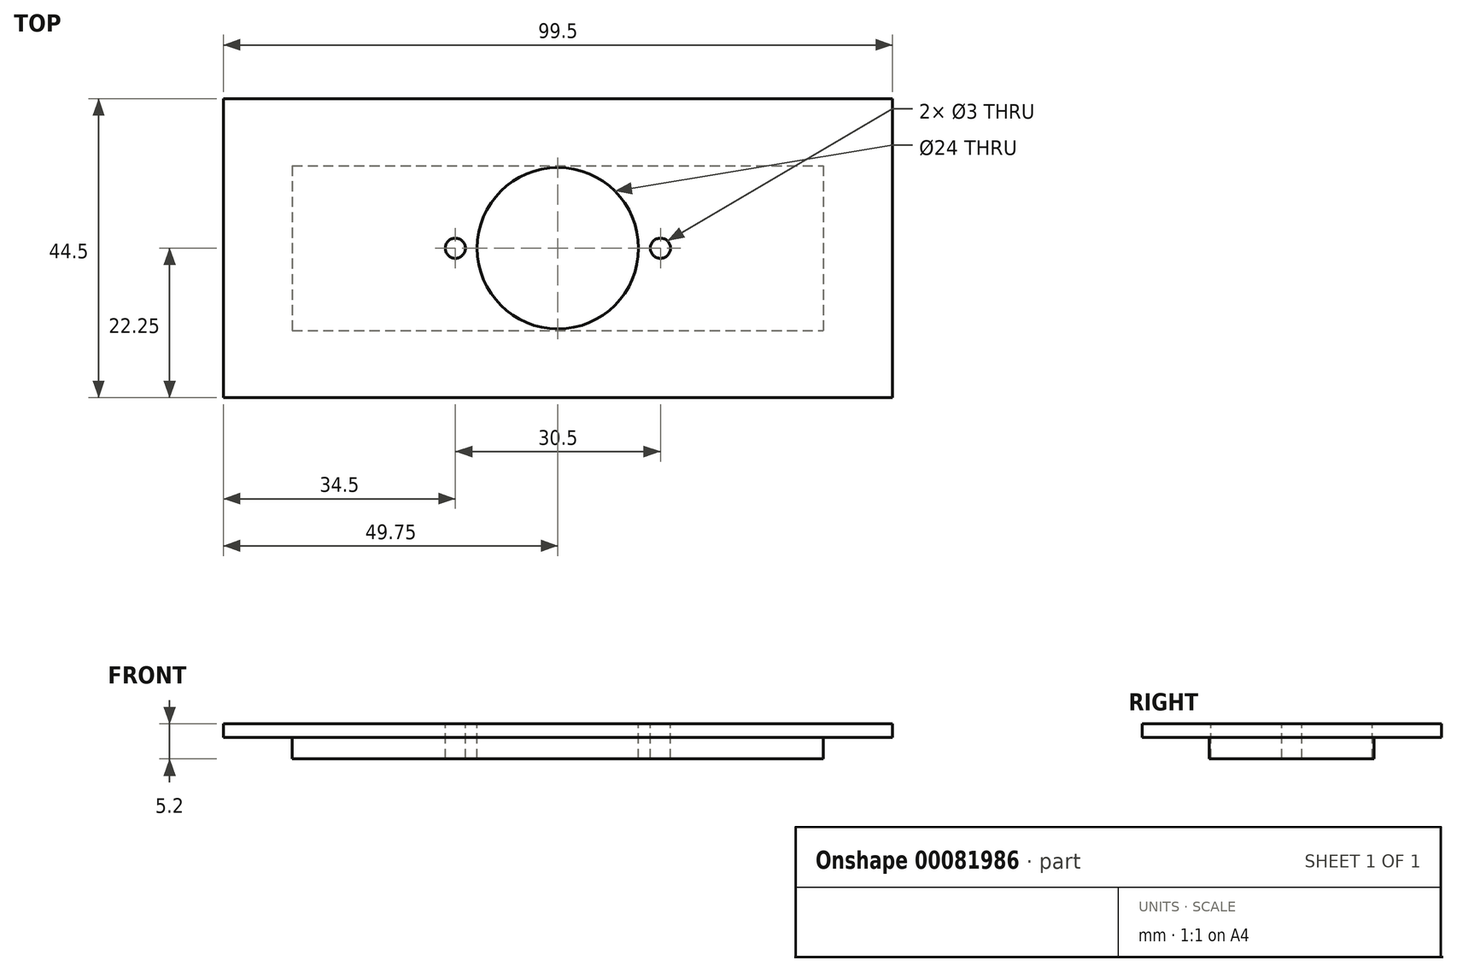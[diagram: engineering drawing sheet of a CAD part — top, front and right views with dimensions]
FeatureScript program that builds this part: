
annotation { "Feature Type Name" : "Feature", "Feature Type Description" : "" }
export const myFeature = defineFeature(function(context is Context, id is Id, definition is map)
    precondition{}
    {
        {
            var Q0;
            Q0=qCreatedBy(makeId("Top.planeOp"),FACE);
            var sketch = newSketch(context, id + "F0", { "sketchPlane" : qUnion([Q0])});
            skLineSegment(sketch, "E0.bottom", {"start": v(-39.5, 12.25) * mm, "end": v(39.5, 12.25) * mm});
            skLineSegment(sketch, "E0.top", {"start": v(-39.5, -12.25) * mm, "end": v(39.5, -12.25) * mm});
            skLineSegment(sketch, "E0.left", {"start": v(-39.5, 12.25) * mm, "end": v(-39.5, -12.25) * mm});
            skLineSegment(sketch, "E0.right", {"start": v(39.5, 12.25) * mm, "end": v(39.5, -12.25) * mm});
            skPoint(sketch, "E0.middle", {"position": v(0, 0) * mm});
            skSolve(sketch);
        }
        {
            var Q0;
            Q0 = qSketchRegion(id + "F0", true);
            extrude(context, id + "F1", {"entities" : qUnion([Q0]), "depth" : 3.2 * mm});
        }
        {
            var Q0;
            Q0=makeQuery(id+"F1.opExtrude","CAP_FACE",FACE,{"disambiguationData":[OSD([sQuery(id+"F0.wireOp",EDGE,"E0.bottom"),sQuery(id+"F0.wireOp",EDGE,"E0.top"),sQuery(id+"F0.wireOp",EDGE,"E0.left"),sQuery(id+"F0.wireOp",EDGE,"E0.right")])],"isStart":false});
            var sketch = newSketch(context, id + "F2", { "sketchPlane" : qUnion([Q0])});
            skLineSegment(sketch, "E1.bottom", {"start": v(-49.75, 22.25) * mm, "end": v(49.75, 22.25) * mm});
            skLineSegment(sketch, "E1.top", {"start": v(-49.75, -22.25) * mm, "end": v(49.75, -22.25) * mm});
            skLineSegment(sketch, "E1.left", {"start": v(-49.75, 22.25) * mm, "end": v(-49.75, -22.25) * mm});
            skLineSegment(sketch, "E1.right", {"start": v(49.75, 22.25) * mm, "end": v(49.75, -22.25) * mm});
            skPoint(sketch, "E1.middle", {"position": v(0, 0) * mm});
            skSolve(sketch);
        }
        {
            var Q0;
            Q0 = qSketchRegion(id + "F2", true);
            extrude(context, id + "F3", {"entities" : qUnion([Q0]), "operationType" : NewBodyOperationType.ADD, "depth" : 2 * mm});
        }
        {
            var Q0;
            Q0=makeQuery(id+"F3.opExtrude","CAP_FACE",FACE,{"disambiguationData":[OSD([sQuery(id+"F2.wireOp",EDGE,"E1.bottom"),sQuery(id+"F2.wireOp",EDGE,"E1.top"),sQuery(id+"F2.wireOp",EDGE,"E1.left"),sQuery(id+"F2.wireOp",EDGE,"E1.right")])],"isStart":false});
            var sketch = newSketch(context, id + "F4", { "sketchPlane" : qUnion([Q0])});
            skCircle(sketch, "E2", {"center": v(0, 0) * mm, "radius": 12 * mm});
            skLineSegment(sketch, "E3", {"start": v(-15.25, 0) * mm, "end": v(15.25, 0) * mm, "construction": true});
            skCircle(sketch, "E4", {"center": v(-15.25, 0) * mm, "radius": 1.5 * mm});
            skCircle(sketch, "E5", {"center": v(15.25, 0) * mm, "radius": 1.5 * mm});
            skSolve(sketch);
        }
        {
            var Q0;
            Q0 = qSketchRegion(id + "F4", true);
            var Q1;
            Q1=makeQuery(id+"F1.opExtrude","CAP_FACE",FACE,{"disambiguationData":[OSD([sQuery(id+"F0.wireOp",EDGE,"E0.bottom"),sQuery(id+"F0.wireOp",EDGE,"E0.top"),sQuery(id+"F0.wireOp",EDGE,"E0.left"),sQuery(id+"F0.wireOp",EDGE,"E0.right")])],"isStart":true});
            extrude(context, id + "F5", {"entities" : qUnion([Q0]), "operationType" : NewBodyOperationType.REMOVE, "endBound" : BoundingType.UP_TO_SURFACE, "oppositeDirection" : true, "endBoundEntityFace" : qUnion([Q1]), "depth" : 25 * mm});
        }
    });
